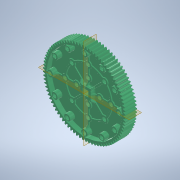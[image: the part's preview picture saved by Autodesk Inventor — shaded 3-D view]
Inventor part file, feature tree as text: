
AUTODESK INVENTOR PART (.ipt)
format: ipt  version: 2020 (Build 240168000, 168)  size: 7,859,200 bytes
history: native  units: in
note: dims shown in document units (in); Inventor stores cm internally (conversion verified against a paired STEP export)
features: other x3, plane x2, boolean_combine x1, imported_body x1
ambient origin geometry x8: Origin, YZ Plane, XZ Plane, XY Plane, X Axis, Y Axis, Z Axis, Center Point
bodies: Body1 (feature_tree)
feature tree (7):
  other  "Gear HS 84 tooth"
  boolean_combine  "Combine1"
  other  "Gear HS"
  other  "Work Axis1"
  imported_body  "Base1"
  plane  "Work Plane1"
  plane  "Work Plane2"
